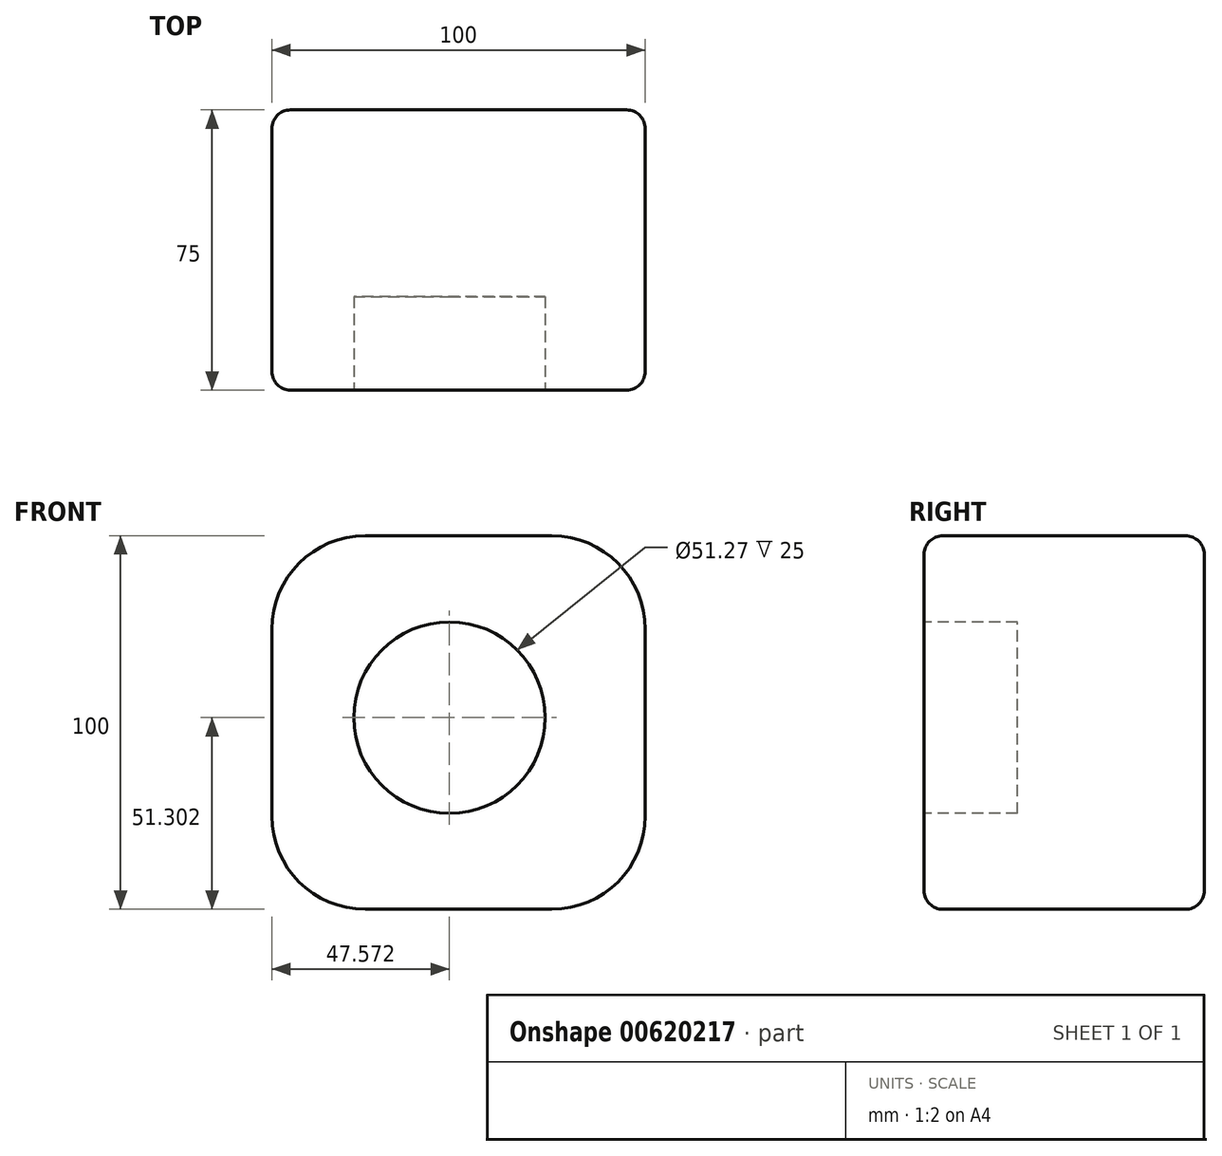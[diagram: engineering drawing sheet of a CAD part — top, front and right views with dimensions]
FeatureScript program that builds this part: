
annotation { "Feature Type Name" : "Feature", "Feature Type Description" : "" }
export const myFeature = defineFeature(function(context is Context, id is Id, definition is map)
    precondition{}
    {
        {
            var Q0;
            Q0=qCreatedBy(makeId("Front.planeOp"),FACE);
            var sketch = newSketch(context, id + "F0", { "sketchPlane" : qUnion([Q0])});
            skLineSegment(sketch, "E0.bottom", {"start": v(-25.6, 77.7) * mm, "end": v(24.4, 77.7) * mm});
            skLineSegment(sketch, "E0.top", {"start": v(-25.6, -22.3) * mm, "end": v(24.4, -22.3) * mm});
            skLineSegment(sketch, "E0.left", {"start": v(-50.6, 52.7) * mm, "end": v(-50.6, 2.7) * mm});
            skLineSegment(sketch, "E0.right", {"start": v(49.4, 52.7) * mm, "end": v(49.4, 2.7) * mm});
            skPoint(sketch, "E1.visualSharp", {"position": v(-50.6, 77.7) * mm});
            skArc(sketch, "E1.filletArc", {"start": v(-25.6, 77.7) * mm, "mid": v(-43.27, 70.37) * mm, "end": v(-50.6, 52.7) * mm});
            skPoint(sketch, "E2.visualSharp", {"position": v(49.4, -22.3) * mm});
            skArc(sketch, "E2.filletArc", {"start": v(24.4, -22.3) * mm, "mid": v(42.08, -14.99) * mm, "end": v(49.4, 2.7) * mm});
            skPoint(sketch, "E3.visualSharp", {"position": v(49.4, 77.7) * mm});
            skArc(sketch, "E3.filletArc", {"start": v(49.4, 52.7) * mm, "mid": v(42.08, 70.37) * mm, "end": v(24.4, 77.7) * mm});
            skPoint(sketch, "E4.visualSharp", {"position": v(-50.6, -22.3) * mm});
            skArc(sketch, "E4.filletArc", {"start": v(-50.6, 2.7) * mm, "mid": v(-43.27, -14.99) * mm, "end": v(-25.6, -22.3) * mm});
            skSolve(sketch);
        }
        {
            var Q0;
            Q0 = qSketchRegion(id + "F0", true);
            extrude(context, id + "F1", {"entities" : qUnion([Q0]), "depth" : 75 * mm, "offsetDistance" : 25 * mm});
        }
        {
            var Q0;
            Q0=makeQuery(id+"F1.opExtrude","SWEPT_EDGE",EDGE,{"disambiguationData":[OSD([sQuery(id+"F0.wireOp",EDGE,"E0.bottom"),sQuery(id+"F0.wireOp",EDGE,"E3.filletArc")])]});
            var Q1;
            Q1=makeQuery(id+"F1.opExtrude","CAP_EDGE",EDGE,{"disambiguationData":[OSD([sQuery(id+"F0.wireOp",EDGE,"E0.bottom")])],"isStart":false});
            var Q2;
            Q2=makeQuery(id+"F1.opExtrude","CAP_EDGE",EDGE,{"disambiguationData":[OSD([sQuery(id+"F0.wireOp",EDGE,"E3.filletArc")])],"isStart":false});
            var Q3;
            Q3=makeQuery(id+"F1.opExtrude","SWEPT_EDGE",EDGE,{"disambiguationData":[OSD([sQuery(id+"F0.wireOp",EDGE,"E0.left"),sQuery(id+"F0.wireOp",EDGE,"E4.filletArc")])]});
            var Q4;
            Q4=makeQuery(id+"F1.opExtrude","CAP_EDGE",EDGE,{"disambiguationData":[OSD([sQuery(id+"F0.wireOp",EDGE,"E0.left")])],"isStart":true});
            var Q5;
            Q5=makeQuery(id+"F1.opExtrude","CAP_EDGE",EDGE,{"disambiguationData":[OSD([sQuery(id+"F0.wireOp",EDGE,"E4.filletArc")])],"isStart":true});
            var Q6;
            Q6=makeQuery(id+"F1.opExtrude","CAP_EDGE",EDGE,{"disambiguationData":[OSD([sQuery(id+"F0.wireOp",EDGE,"E3.filletArc")])],"isStart":true});
            var Q7;
            Q7=makeQuery(id+"F1.opExtrude","CAP_FACE",FACE,{"disambiguationData":[OSD([sQuery(id+"F0.wireOp",EDGE,"E0.bottom"),sQuery(id+"F0.wireOp",EDGE,"E0.top"),sQuery(id+"F0.wireOp",EDGE,"E0.left"),sQuery(id+"F0.wireOp",EDGE,"E0.right"),sQuery(id+"F0.wireOp",EDGE,"E1.filletArc"),sQuery(id+"F0.wireOp",EDGE,"E2.filletArc"),sQuery(id+"F0.wireOp",EDGE,"E3.filletArc"),sQuery(id+"F0.wireOp",EDGE,"E4.filletArc")])],"isStart":true});
            fillet(context, id + "F2", {"entities" : qUnion([Q0, Q1, Q2, Q3, Q4, Q5, Q6, Q7]), "radius" : 5 * mm, "tangentPropagation" : true, "allowEdgeOverflow" : false});
        }
        {
            var Q0;
            Q0=makeQuery(id+"F1.opExtrude","CAP_FACE",FACE,{"disambiguationData":[OSD([sQuery(id+"F0.wireOp",EDGE,"E0.bottom"),sQuery(id+"F0.wireOp",EDGE,"E0.top"),sQuery(id+"F0.wireOp",EDGE,"E0.left"),sQuery(id+"F0.wireOp",EDGE,"E0.right"),sQuery(id+"F0.wireOp",EDGE,"E1.filletArc"),sQuery(id+"F0.wireOp",EDGE,"E2.filletArc"),sQuery(id+"F0.wireOp",EDGE,"E3.filletArc"),sQuery(id+"F0.wireOp",EDGE,"E4.filletArc")])],"isStart":false});
            var sketch = newSketch(context, id + "F3", { "sketchPlane" : qUnion([Q0])});
            skCircle(sketch, "E5", {"center": v(-3.02, 29) * mm, "radius": 25.64 * mm});
            skSolve(sketch);
        }
        {
            var Q0;
            Q0 = qSketchRegion(id + "F3", true);
            extrude(context, id + "F4", {"entities" : qUnion([Q0]), "operationType" : NewBodyOperationType.REMOVE, "oppositeDirection" : true, "depth" : 25 * mm, "offsetDistance" : 25 * mm});
        }
    });
